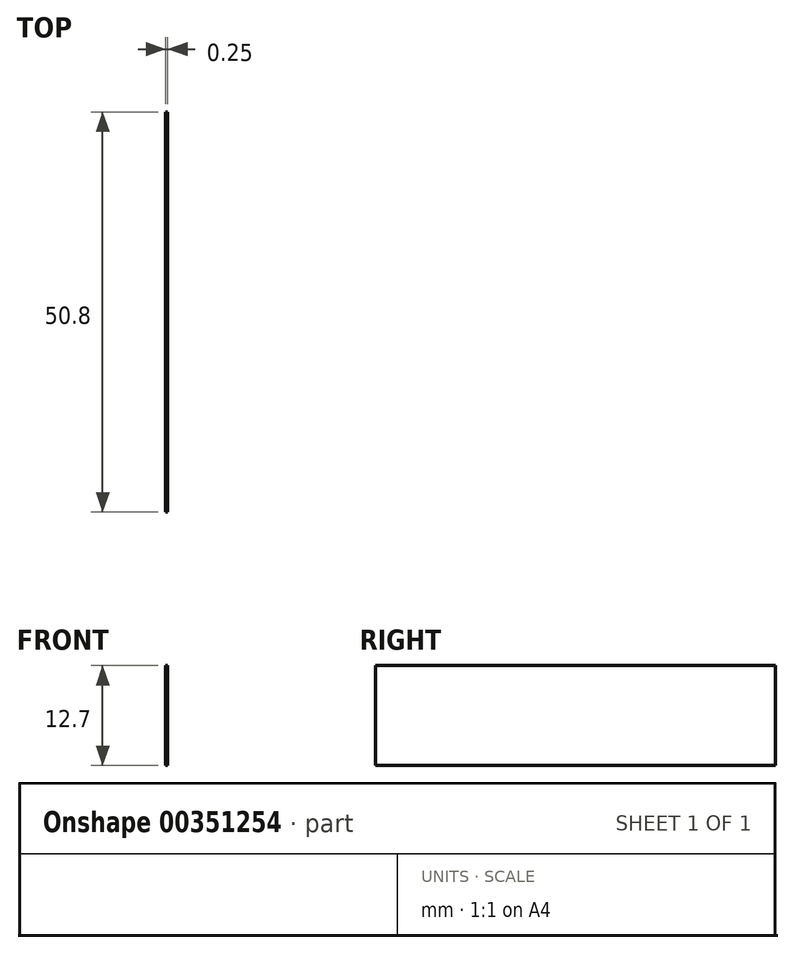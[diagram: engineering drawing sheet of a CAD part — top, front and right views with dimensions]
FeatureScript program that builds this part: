
annotation { "Feature Type Name" : "Feature", "Feature Type Description" : "" }
export const myFeature = defineFeature(function(context is Context, id is Id, definition is map)
    precondition{}
    {
        {
            var Q0;
            Q0=qCreatedBy(makeId("Right.planeOp"),FACE);
            var sketch = newSketch(context, id + "F0", { "sketchPlane" : qUnion([Q0])});
            skLineSegment(sketch, "E0.bottom", {"start": v(-27.58, -1.44) * mm, "end": v(23.22, -1.44) * mm});
            skLineSegment(sketch, "E0.top", {"start": v(-27.58, -14.14) * mm, "end": v(23.22, -14.14) * mm});
            skLineSegment(sketch, "E0.left", {"start": v(-27.58, -1.44) * mm, "end": v(-27.58, -14.14) * mm});
            skLineSegment(sketch, "E0.right", {"start": v(23.22, -1.44) * mm, "end": v(23.22, -14.14) * mm});
            skSolve(sketch);
        }
        {
            var Q0;
            Q0=makeQuery(id+"F0.imprint","IMPRINT",FACE,{"disambiguationData":[TD([[makeQuery(id+"F0.imprint","IMPRINT",EDGE,{"derivedFrom":sQuery(id+"F0.wireOp",EDGE,"E0.bottom")}),-1.0]])]});
            extrude(context, id + "F1", {"entities" : qUnion([Q0]), "depth" : 0.25 * mm});
        }
    });
